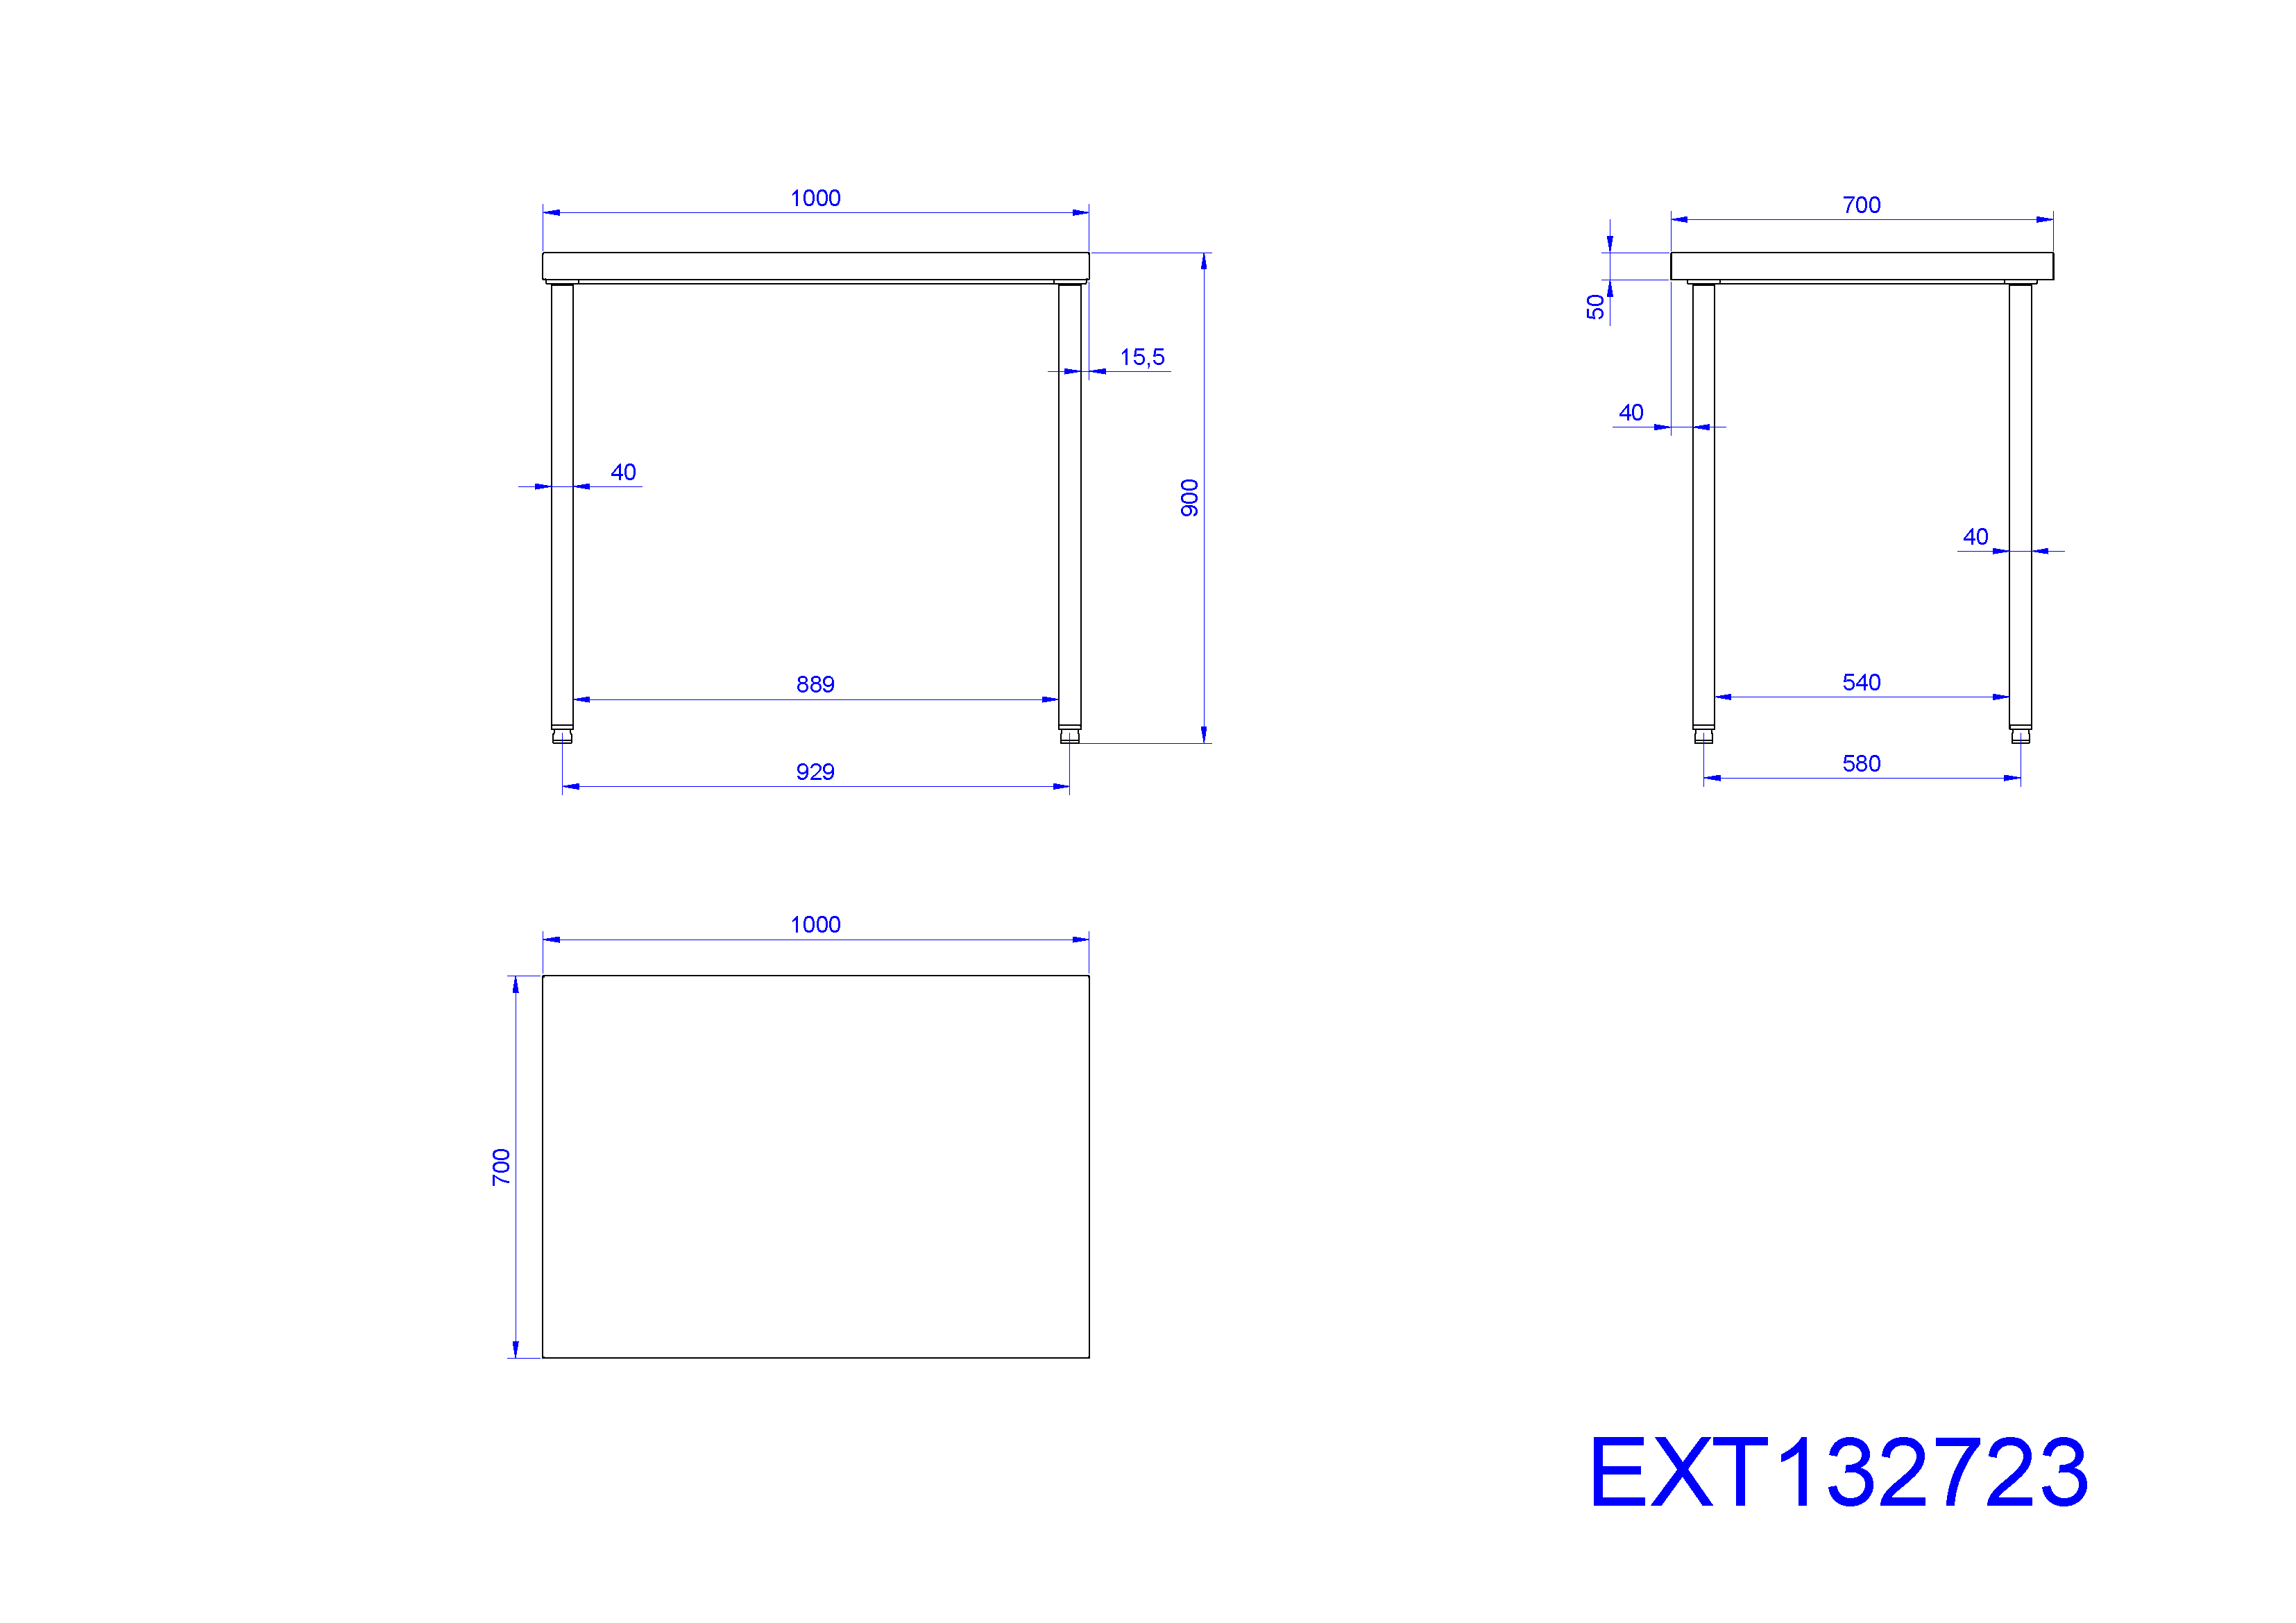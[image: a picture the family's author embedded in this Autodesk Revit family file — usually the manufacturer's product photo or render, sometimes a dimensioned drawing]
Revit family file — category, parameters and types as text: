
# Revit family: QF_ELECTROLUXPROFESSIONAL_132727_TG1800PN
name_source: partatom
category: Attrezzature speciali
units: mm (PartAtom-declared; Revit-internal decimal feet)

## family parameters
Basato su piano di lavoro = No
Condiviso = No
Punto di calcolo locali = No
Quota connettore circolare = Usa diametro
Sempre verticale = Sì
Taglio con vuoti quando caricato = No
Tipo di parte = Normale

## types (1)
- Standard
    Accessory = Sì
    Cold Water Size = 0 mm
    Compressed Air Pressure = 0.0 Pa
    Compressed Air Size = 0 mm
    Compressed Air Volume = 0.0 L/s
    Condensate Return Size = 0 mm
    Cycle = 0 Hz
    Depth Actual = 700 mm  [stored 2.29659 ft]
    Descrizione = WORK TABLE 1800 MM
    Direct Waste Size = 0 mm
    Gas Input Pressure = 0
    Gas KW = 0
    Gas Size = 0 mm
    HP = 0 HP
    Height Actual = 900 mm  [stored 2.95276 ft]
    Hot Water Size = 0 mm
    Item Number = 132727
    Length Actual = 1800 mm  [stored 5.90551 ft]
    Modello = TG1800PN
    Phase = 0
    Produttore = Electrolux Professional
    Prospetto di default = 0 mm  [stored 0 ft]
    Refrigerant Compressor Remote = Sì
    Refrigeration Liquid Line Size = 0 mm  [stored 0 ft]
    Refrigeration Suction Line Size = 0 mm  [stored 0 ft]
    Steam Consumption per Hour = 0
    Steam Supply Maximum Pressure = 0.0 Pa
    Steam Supply Minimum Pressure = 0.0 Pa
    Steam Supply Size = 0 mm
    URL = https://www.electroluxprofessional.com
    URL Manufacturer = https://www.electroluxprofessional.com
    Volts = 0 V
    Watts = 0 W
    Weight = 54.00 kg

note: source unit labels omitted for Gas Input Pressure — the stored unit's dimension contradicts the parameter name (converter mislabeling)

note: [stored X ft] marks values corroborated as IEEE doubles in the binary element streams (Revit-internal decimal feet)

## geometry (parser evidence)
native form markers: Sweep x2
no freeform markers — native parametric forms only
